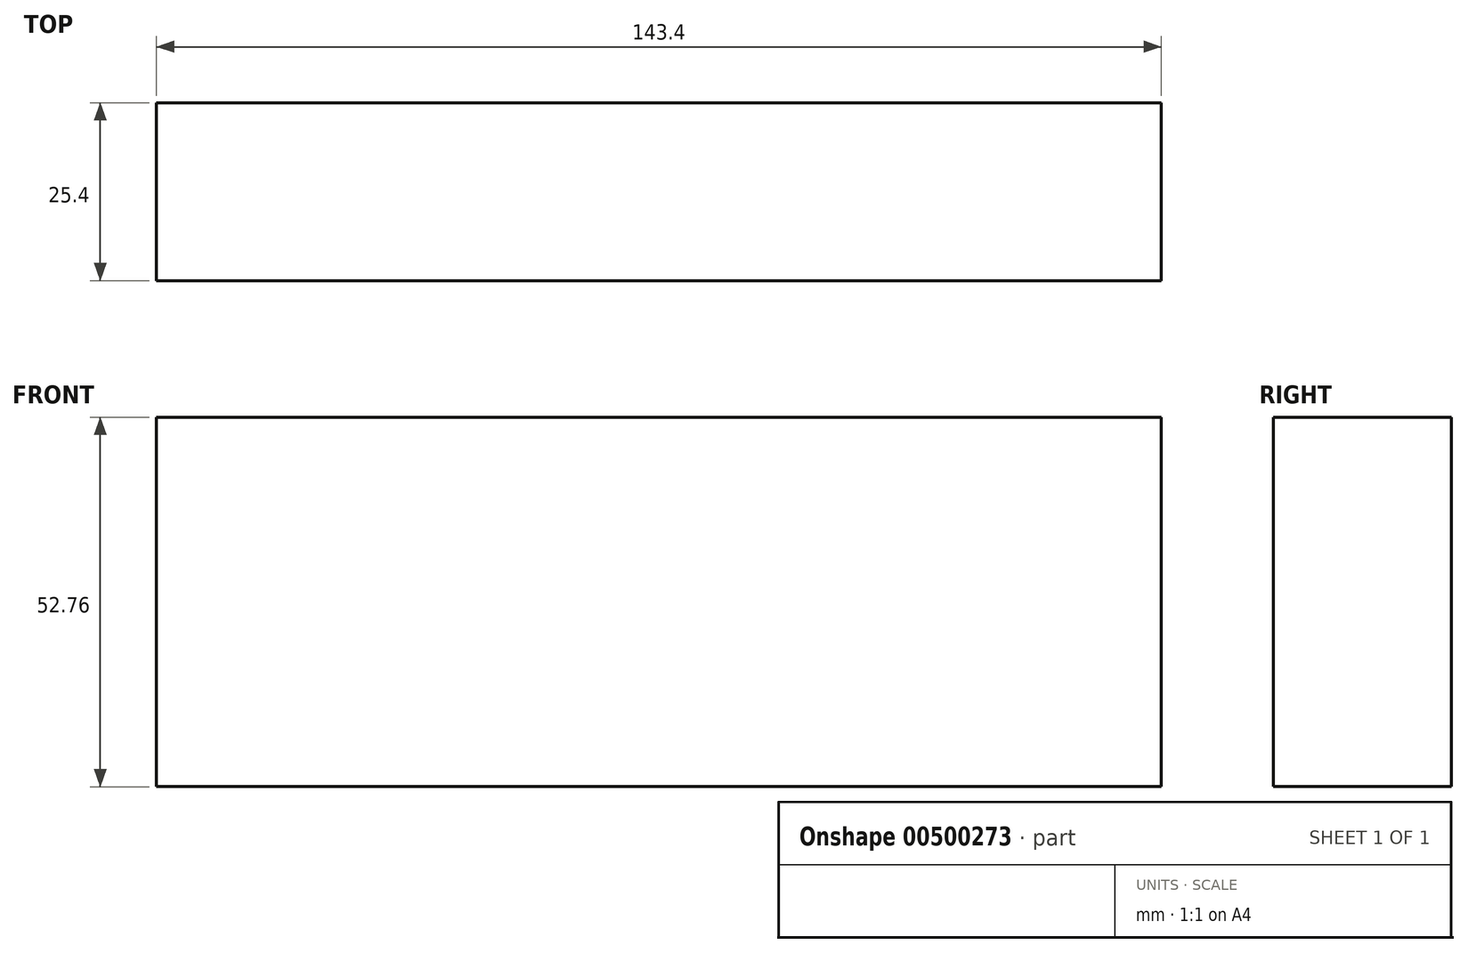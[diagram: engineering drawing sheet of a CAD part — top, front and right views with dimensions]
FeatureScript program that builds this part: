
annotation { "Feature Type Name" : "Feature", "Feature Type Description" : "" }
export const myFeature = defineFeature(function(context is Context, id is Id, definition is map)
    precondition{}
    {
        {
            var Q0;
            Q0=qCreatedBy(makeId("Front.planeOp"),FACE);
            var sketch = newSketch(context, id + "F0", { "sketchPlane" : qUnion([Q0])});
            skLineSegment(sketch, "E0.bottom", {"start": v(71.7, 26.38) * mm, "end": v(-71.7, 26.38) * mm});
            skLineSegment(sketch, "E0.top", {"start": v(71.7, -26.38) * mm, "end": v(-71.7, -26.38) * mm});
            skLineSegment(sketch, "E0.left", {"start": v(71.7, 26.38) * mm, "end": v(71.7, -26.38) * mm});
            skLineSegment(sketch, "E0.right", {"start": v(-71.7, 26.38) * mm, "end": v(-71.7, -26.38) * mm});
            skPoint(sketch, "E0.middle", {"position": v(0, 0) * mm});
            skSolve(sketch);
        }
        {
            var Q0;
            Q0=makeQuery(id+"F0.imprint","IMPRINT",FACE,{"disambiguationData":[TD([[makeQuery(id+"F0.imprint","IMPRINT",EDGE,{"derivedFrom":sQuery(id+"F0.wireOp",EDGE,"E0.bottom")}),1.0]])]});
            extrude(context, id + "F1", {"entities" : qUnion([Q0]), "depth" : 25.4 * mm});
        }
    });
